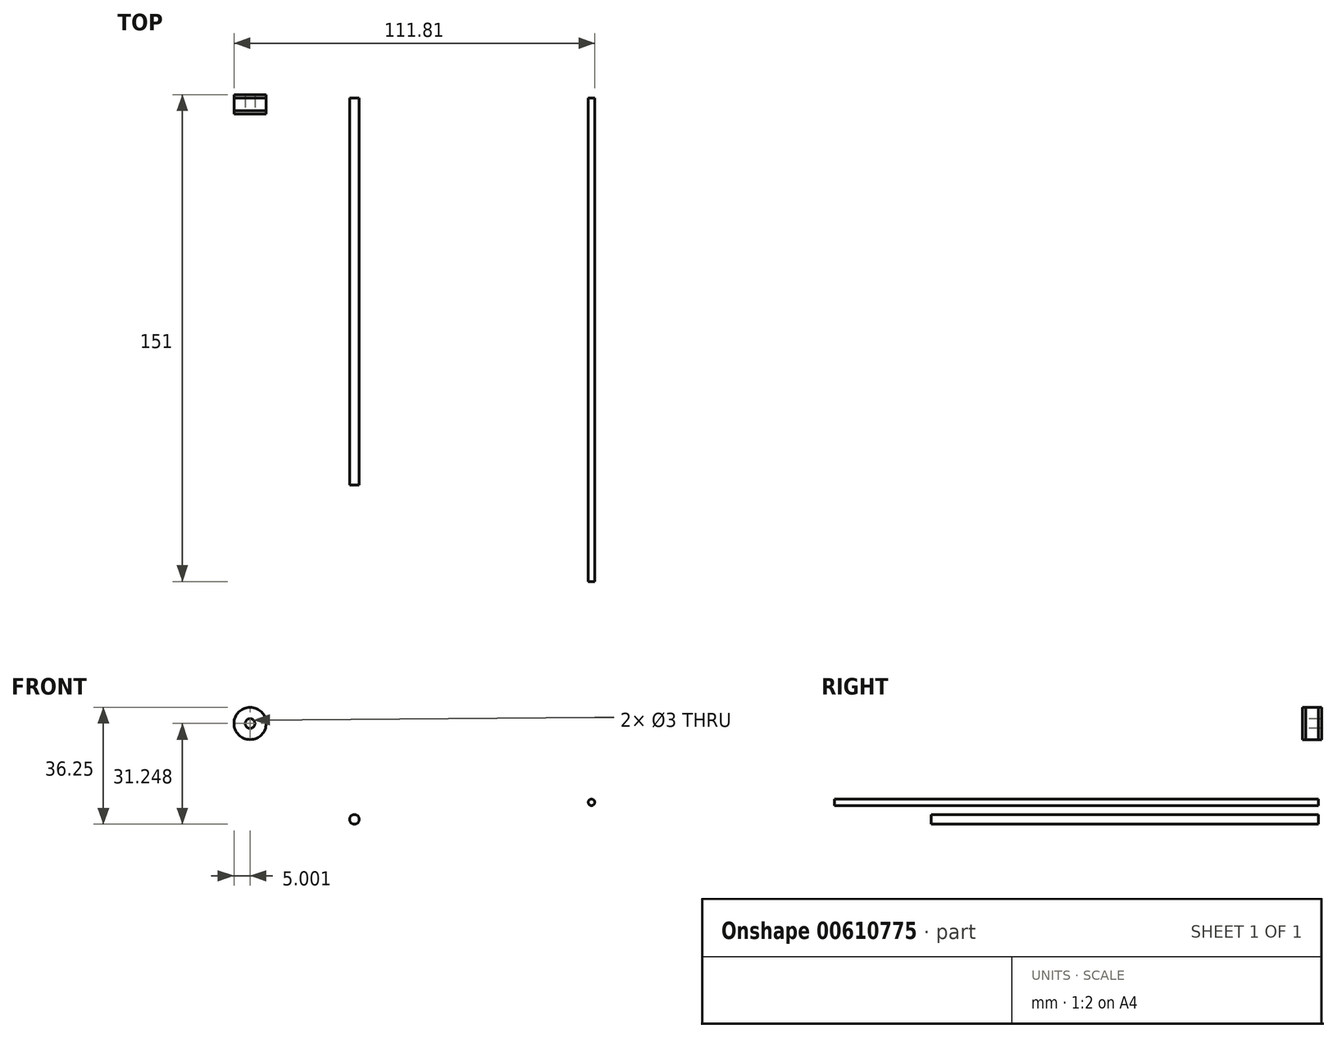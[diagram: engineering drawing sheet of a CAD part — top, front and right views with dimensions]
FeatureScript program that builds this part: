
annotation { "Feature Type Name" : "Feature", "Feature Type Description" : "" }
export const myFeature = defineFeature(function(context is Context, id is Id, definition is map)
    precondition{}
    {
        {
            var Q0;
            Q0=qCreatedBy(makeId("Front.planeOp"),FACE);
            var sketch = newSketch(context, id + "F0", { "sketchPlane" : qUnion([Q0])});
            skCircle(sketch, "E0", {"center": v(-25.79, 20.17) * mm, "radius": 1.5 * mm});
            skSolve(sketch);
        }
        {
            var Q0;
            Q0 = qSketchRegion(id + "F0", true);
            extrude(context, id + "F1", {"entities" : qUnion([Q0]), "depth" : 120 * mm, "offsetDistance" : 25 * mm});
        }
        {
            var Q0;
            Q0=qCreatedBy(makeId("Front.planeOp"),FACE);
            var sketch = newSketch(context, id + "F2", { "sketchPlane" : qUnion([Q0])});
            skCircle(sketch, "E1", {"center": v(-58.13, 49.92) * mm, "radius": 5 * mm});
            skSolve(sketch);
        }
        {
            var Q0;
            Q0 = qSketchRegion(id + "F2", true);
            extrude(context, id + "F3", {"entities" : qUnion([Q0]), "depth" : 5 * mm, "offsetDistance" : 25 * mm});
        }
        {
            var Q0;
            Q0=makeQuery(id+"F3.opExtrude","CAP_FACE",FACE,{"disambiguationData":[OSD([sQuery(id+"F2.wireOp",EDGE,"E1")])],"isStart":false});
            var sketch = newSketch(context, id + "F4", { "sketchPlane" : qUnion([Q0])});
            skCircle(sketch, "E2", {"center": v(-58.13, 49.92) * mm, "radius": 1.5 * mm});
            skSolve(sketch);
        }
        {
            var Q0;
            Q0=sQuery(id+"F4.wireOp",VERTEX,"E2.center");
            var Q1;
            Q1=makeQuery(id+"F3.opExtrude","SWEPT_BODY",BODY,{"disambiguationData":[OSD([sQuery(id+"F2.wireOp",EDGE,"E1")])]});
            hole(context, id + "F5", {"style" : HoleStyle.SIMPLE, "endStyle" : HoleEndStyle.THROUGH, "holeDiameter" : 3 * mm, "majorDiameter" : 5 * mm, "isTappedThrough" : true, "tappedDepth" : 12 * mm, "tapClearance" : 3, "locations" : qUnion([Q0]), "scope" : qUnion([Q1])});
        }
        {
            var Q0;
            Q0=makeQuery(id+"F3.opExtrude","SWEPT_BODY",BODY,{"disambiguationData":[OSD([sQuery(id+"F2.wireOp",EDGE,"E1")])]});
            transform(context, id + "F6", {"entities" : qUnion([Q0]), "transformType" : TransformType.TRANSLATION_3D, "dx" : 0 * mm, "dy" : mm, "dz" : 0 * mm, "makeCopy" : true});
        }
        {
            var Q0;
            Q0=qCreatedBy(makeId("Front.planeOp"),FACE);
            var sketch = newSketch(context, id + "F7", { "sketchPlane" : qUnion([Q0])});
            skCircle(sketch, "E3", {"center": v(47.68, 25.47) * mm, "radius": 1 * mm});
            skSolve(sketch);
        }
        {
            var Q0;
            Q0 = qSketchRegion(id + "F7", true);
            extrude(context, id + "F8", {"entities" : qUnion([Q0]), "depth" : 150 * mm, "offsetDistance" : 25 * mm});
        }
    });
